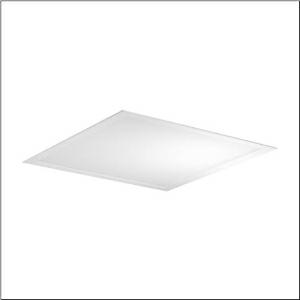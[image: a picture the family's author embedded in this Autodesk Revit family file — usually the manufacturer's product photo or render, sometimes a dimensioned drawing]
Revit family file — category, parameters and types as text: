
# Revit family: apollon_r__31_square_51mp11wd2n42_7747
name_source: partatom
category: Lighting Fixtures
units: mm (PartAtom-declared; Revit-internal decimal feet)

## family parameters
Cut with Voids When Loaded = No
Host = Face
Light Source = No
Part Type = Normal
Room Calculation Point = No
Round Connector Dimension = Use Diameter
Shared = No

## types (1)
- --- (1 x LED, 4000 lm, 27.5 W, 5000K)
    Apparent Load = 28 VA
    CIE Flux Codes = 62 87 97 100 100
    Color Rendering = 80
    Color Temperature = 5000K
    Default Elevation = 1800 mm
    Description = Apollon® 31 square, office luminaire, primary optical cover: micro prismatic cover, of PMMA, CAT 2 (L<= 3000cd/m²), light emission: direct distribution, primary light characteristic: symmetric, installation type: lay-in mounting, LED, rated luminous flux: 4.000lm, luminous efficacy: 145lm/W, light colour: 840/850, colour temperature: 4000/5000K, control gear: DALI 2, Multilumen, with terminal, 5-pole, mains connection: 220..240V, AC/DC, 0/50..60Hz, rated input power: 28W, housing, of aluminium, traffic white (RAL 9016), module: M625, length: 620mm, width: 620mm, height: 62mm, recess depth: 180mm, housing upper side, of sheet steel, coated, protection rating (complete): IP20, protection rating (on room side): IP40, insulation class (complete): insulation class II (safety insulation), certification: CE, ENEC, impact resistance: IK03, permissible operating ambient temperature: -20..+40°C, permissible storage temperature: -20..+60°C, standard: EN 60598-2-22, packaging unit: 1 piece
    Height = 0 mm  [stored 0 ft]
    Lamp = 1 x LED
    Lamp Light Flux = 4000 lm
    Lamp Power = 27.5 W
    Lamp count = 1
    Length = 620 mm
    Luminous efficacy = 145 lm/W
    Manufacturer = Siteco
    ModVariant = No
    Model = 51MP11WD2N42
    Mounting Place = Ceiling
    Mounting Type = Recessed
    Number of Poles = 1
    OnlyDefault = Yes
    Power Factor = 1
    Product Name = Apollon® 31 square
    Product group = office luminaire | ceiling recessed
    ProductGroupID = 401
    Protection Class = Protection class II
    Protection Degree = IP 20
    RLX_Detail_Level = 1
    RLX_Emergency_Light_Flux = 0 lm
    RLX_Emergency_Type = 0
    RLX_Emergency_Type_DB = No
    RlxData = <blob elided: 13249 chars, md5=c2449925>
    Socket = socket
    Standby Power = 0 W
    System Light Flux = 4000 lm
    System Power = 28 W
    Type Comments = individual setting: colour temperature 5000K
    Type Image = l_1291039.jpg
    URL = http://relux.com
    VarID = @adj_076632
    Voltage = 0 V
    Weight = 0.00 kg
    Width = 620 mm

note: [stored X ft] marks values corroborated as IEEE doubles in the binary element streams (Revit-internal decimal feet)

## geometry (parser evidence)
native form markers: Sweep x10
no freeform markers — native parametric forms only
